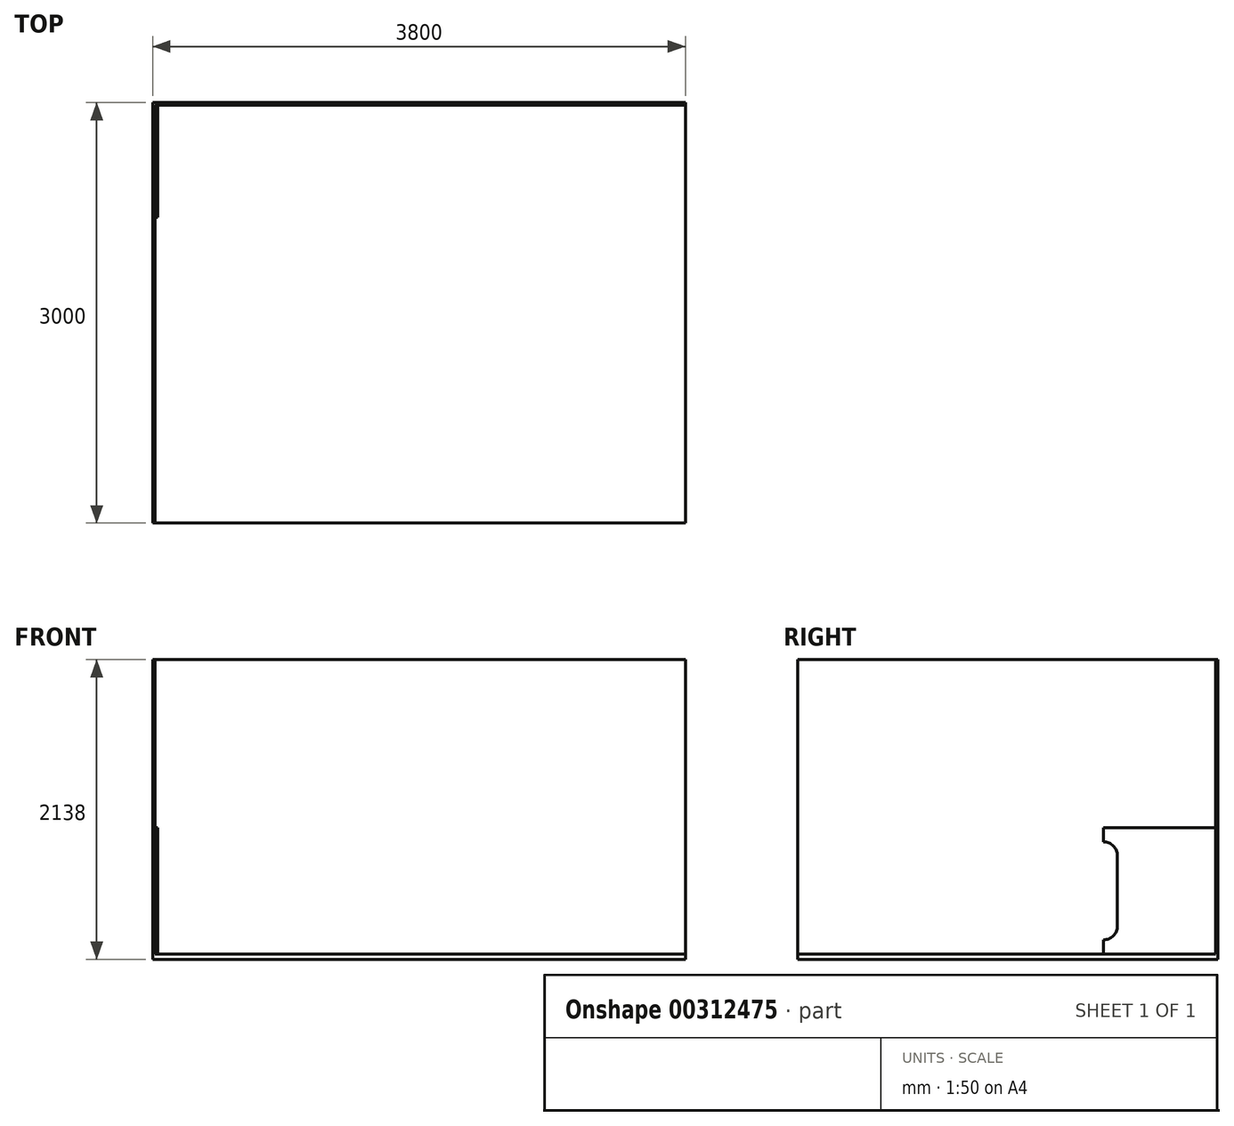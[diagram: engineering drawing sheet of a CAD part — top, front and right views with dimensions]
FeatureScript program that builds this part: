
annotation { "Feature Type Name" : "Feature", "Feature Type Description" : "" }
export const myFeature = defineFeature(function(context is Context, id is Id, definition is map)
    precondition{}
    {
        {
            var Q0;
            Q0=qCreatedBy(makeId("Top.planeOp"),FACE);
            var sketch = newSketch(context, id + "F0", { "sketchPlane" : qUnion([Q0])});
            skLineSegment(sketch, "E0.bottom", {"start": v(0, 0) * mm, "end": v(3800, 0) * mm});
            skLineSegment(sketch, "E0.top", {"start": v(0, -3000) * mm, "end": v(3800, -3000) * mm});
            skLineSegment(sketch, "E0.left", {"start": v(0, 0) * mm, "end": v(0, -3000) * mm});
            skLineSegment(sketch, "E0.right", {"start": v(3800, 0) * mm, "end": v(3800, -3000) * mm});
            skSolve(sketch);
        }
        {
            var Q0;
            Q0=makeQuery(id+"F0.imprint","IMPRINT",FACE,{"disambiguationData":[TD([[makeQuery(id+"F0.imprint","IMPRINT",EDGE,{"derivedFrom":sQuery(id+"F0.wireOp",EDGE,"E0.bottom")}),-1.0]])]});
            extrude(context, id + "F1", {"entities" : qUnion([Q0]), "depth" : 38 * mm});
        }
        {
            var Q0;
            Q0=makeQuery(id+"F1.opExtrude","CAP_FACE",FACE,{"disambiguationData":[OSD([sQuery(id+"F0.wireOp",EDGE,"E0.bottom"),sQuery(id+"F0.wireOp",EDGE,"E0.top"),sQuery(id+"F0.wireOp",EDGE,"E0.left"),sQuery(id+"F0.wireOp",EDGE,"E0.right")])],"isStart":false});
            var sketch = newSketch(context, id + "F2", { "sketchPlane" : qUnion([Q0])});
            skLineSegment(sketch, "E1.bottom", {"start": v(3800, 0) * mm, "end": v(0, 0) * mm});
            skLineSegment(sketch, "E1.top", {"start": v(3800, -18) * mm, "end": v(0, -18) * mm});
            skLineSegment(sketch, "E1.left", {"start": v(3800, 0) * mm, "end": v(3800, -18) * mm});
            skLineSegment(sketch, "E1.right", {"start": v(0, 0) * mm, "end": v(0, -18) * mm});
            skSolve(sketch);
        }
        {
            var Q0;
            Q0 = qSketchRegion(id + "F2", true);
            extrude(context, id + "F3", {"entities" : qUnion([Q0]), "operationType" : NewBodyOperationType.ADD, "depth" : 2100 * mm});
        }
        {
            var Q0;
            Q0=makeQuery(id+"F1.opExtrude","CAP_FACE",FACE,{"disambiguationData":[OSD([sQuery(id+"F0.wireOp",EDGE,"E0.bottom"),sQuery(id+"F0.wireOp",EDGE,"E0.top"),sQuery(id+"F0.wireOp",EDGE,"E0.left"),sQuery(id+"F0.wireOp",EDGE,"E0.right")])],"isStart":false});
            var sketch = newSketch(context, id + "F4", { "sketchPlane" : qUnion([Q0])});
            skLineSegment(sketch, "E2.bottom", {"start": v(0, -3000) * mm, "end": v(18, -3000) * mm});
            skLineSegment(sketch, "E2.top", {"start": v(0, -18) * mm, "end": v(18, -18) * mm});
            skLineSegment(sketch, "E2.left", {"start": v(0, -3000) * mm, "end": v(0, -18) * mm});
            skLineSegment(sketch, "E2.right", {"start": v(18, -3000) * mm, "end": v(18, -18) * mm});
            skSolve(sketch);
        }
        {
            var Q0;
            Q0 = qSketchRegion(id + "F4", true);
            extrude(context, id + "F5", {"entities" : qUnion([Q0]), "operationType" : NewBodyOperationType.ADD, "depth" : 2100 * mm});
        }
        {
            var Q0;
            Q0=makeQuery(id+"F5.opExtrude","SWEPT_FACE",FACE,{"disambiguationData":[OSD([sQuery(id+"F4.wireOp",EDGE,"E2.right")])]});
            var sketch = newSketch(context, id + "F6", { "sketchPlane" : qUnion([Q0])});
            skLineSegment(sketch, "E3.bottom", {"start": v(-818, 38) * mm, "end": v(-18, 38) * mm});
            skLineSegment(sketch, "E3.top", {"start": v(-818, 938) * mm, "end": v(-18, 938) * mm});
            skLineSegment(sketch, "E3.left", {"start": v(-818, 38) * mm, "end": v(-818, 138) * mm});
            skLineSegment(sketch, "E3.right", {"start": v(-18, 38) * mm, "end": v(-18, 938) * mm});
            skPoint(sketch, "E4", {"position": v(-818, 738) * mm});
            skPoint(sketch, "E5", {"position": v(-818, 238) * mm});
            skArc(sketch, "E6", {"start": v(-818, 838) * mm, "mid": v(-747.29, 808.71) * mm, "end": v(-718, 738) * mm});
            skArc(sketch, "E7", {"start": v(-818, 138) * mm, "mid": v(-747.29, 167.29) * mm, "end": v(-718, 238) * mm});
            skLineSegment(sketch, "E8", {"start": v(-718, 738) * mm, "end": v(-718, 238) * mm});
            skLineSegment(sketch, "E9.trimOffspring", {"start": v(-818, 838) * mm, "end": v(-818, 938) * mm});
            skSolve(sketch);
        }
        {
            var Q0;
            Q0=makeQuery(id+"F6.imprint","IMPRINT",FACE,{"disambiguationData":[TD([[makeQuery(id+"F6.imprint","IMPRINT",EDGE,{"derivedFrom":sQuery(id+"F6.wireOp",EDGE,"E3.bottom")}),1.0]])]});
            extrude(context, id + "F7", {"entities" : qUnion([Q0]), "depth" : 18 * mm});
        }
    });
